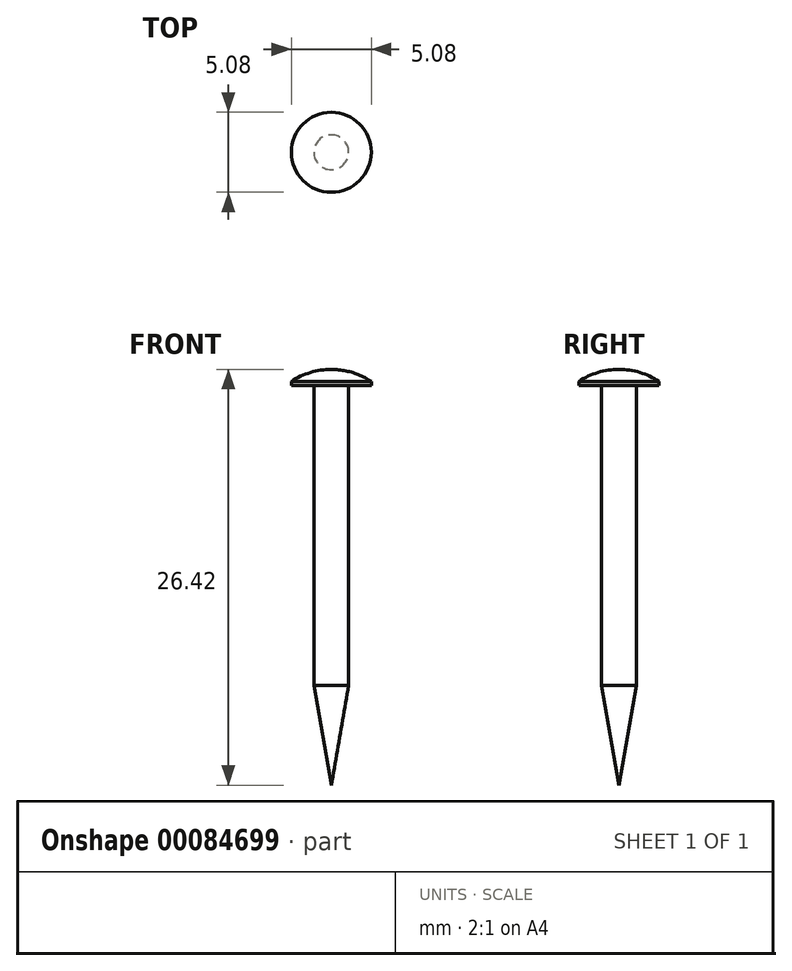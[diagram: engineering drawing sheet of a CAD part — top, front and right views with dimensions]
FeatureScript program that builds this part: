
annotation { "Feature Type Name" : "Feature", "Feature Type Description" : "" }
export const myFeature = defineFeature(function(context is Context, id is Id, definition is map)
    precondition{}
    {
        {
            var Q0;
            Q0=qCreatedBy(makeId("Front.planeOp"),FACE);
            var sketch = newSketch(context, id + "F0", { "sketchPlane" : qUnion([Q0])});
            skLineSegment(sketch, "E0", {"start": v(-1.1, 0) * mm, "end": v(-2.54, 0) * mm});
            skLineSegment(sketch, "E1", {"start": v(-1.1, 0) * mm, "end": v(-1.1, -19.05) * mm});
            skLineSegment(sketch, "E2", {"start": v(-1.1, -19.05) * mm, "end": v(0, -25.4) * mm});
            skLineSegment(sketch, "E3", {"start": v(0, 1.02) * mm, "end": v(0, -25.4) * mm});
            skLineSegment(sketch, "E4", {"start": v(-2.54, 0) * mm, "end": v(-2.54, 0.25) * mm});
            skArc(sketch, "E5", {"start": v(0, 1.02) * mm, "mid": v(-1.33, 0.82) * mm, "end": v(-2.54, 0.25) * mm});
            skSolve(sketch);
        }
        {
            var Q0;
            Q0 = qSketchRegion(id + "F0", true);
            var Q1;
            Q1=sQuery(id+"F0.wireOp",EDGE,"E3");
            revolve(context, id + "F1", {"entities" : qUnion([Q0]), "axis" : qUnion([Q1]), "revolveType" : RevolveType.FULL});
        }
    });
